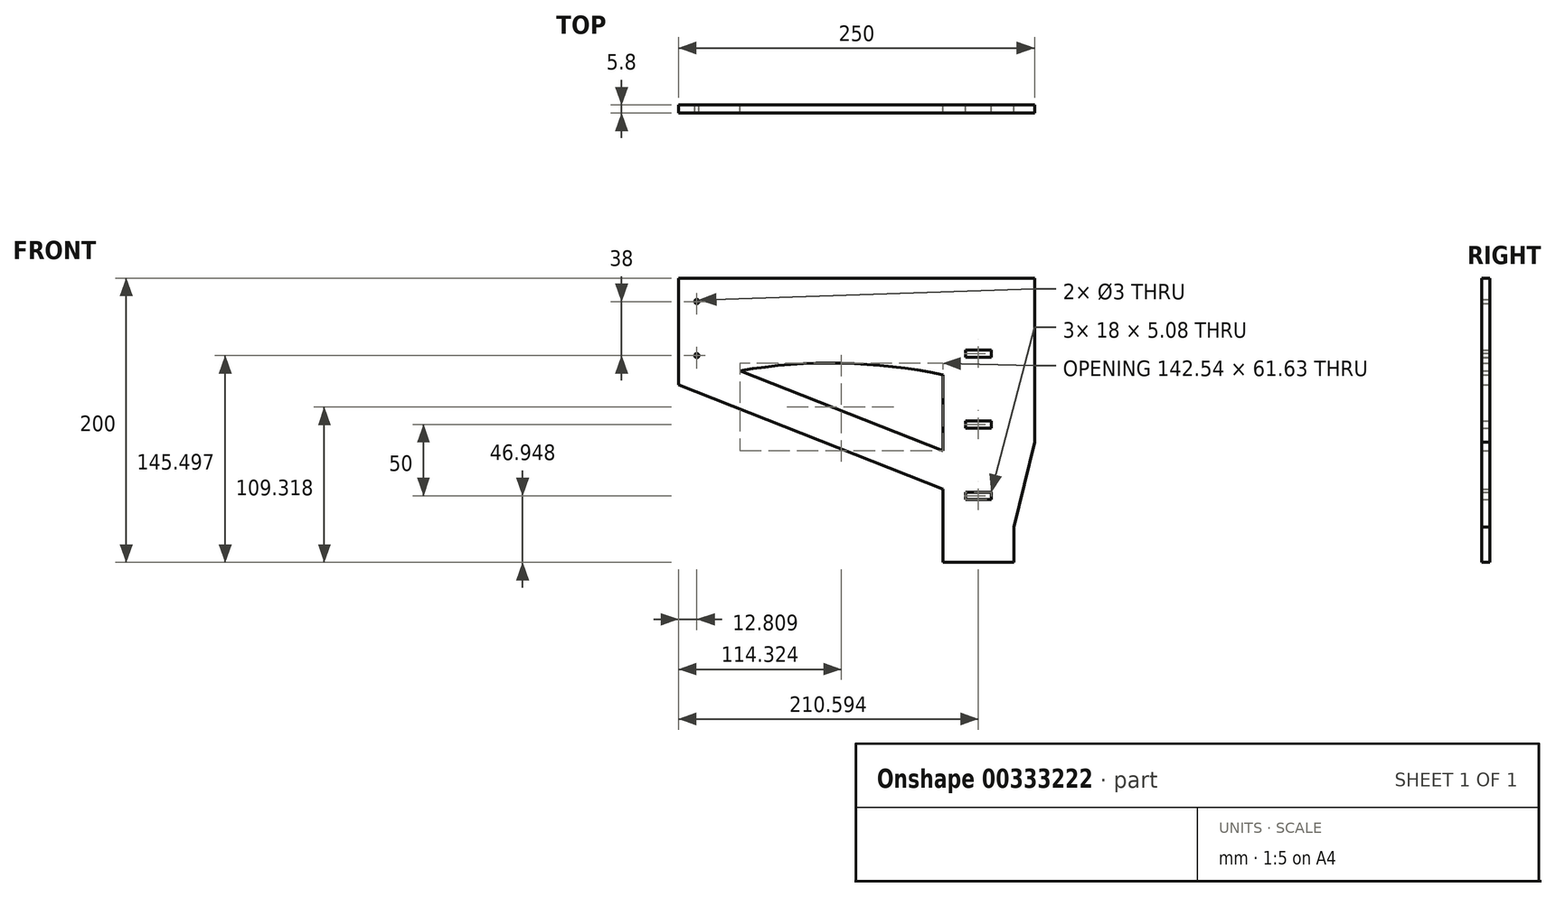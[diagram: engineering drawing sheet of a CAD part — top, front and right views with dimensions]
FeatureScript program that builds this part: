
annotation { "Feature Type Name" : "Feature", "Feature Type Description" : "" }
export const myFeature = defineFeature(function(context is Context, id is Id, definition is map)
    precondition{}
    {
        {
            var Q0;
            Q0=qCreatedBy(makeId("Front.planeOp"),FACE);
            var sketch = newSketch(context, id + "F0", { "sketchPlane" : qUnion([Q0])});
            skLineSegment(sketch, "E0.top", {"start": v(127.28, 55.74) * mm, "end": v(-122.72, 55.74) * mm});
            skLineSegment(sketch, "E0.left", {"start": v(127.28, -59.51) * mm, "end": v(127.28, 55.74) * mm});
            skLineSegment(sketch, "E0.right", {"start": v(-122.72, -19.26) * mm, "end": v(-122.72, 55.74) * mm});
            skArc(sketch, "E1", {"start": v(62.87, -12.25) * mm, "mid": v(-30.35, -4.32) * mm, "end": v(-122.72, -19.26) * mm});
            skPoint(sketch, "E2.orphan", {"position": v(-122.72, -59.51) * mm});
            skLineSegment(sketch, "E3", {"start": v(62.87, -12.25) * mm, "end": v(62.87, -119.26) * mm});
            skLineSegment(sketch, "E4", {"start": v(62.87, -119.26) * mm, "end": v(112.87, -119.26) * mm});
            skLineSegment(sketch, "E5", {"start": v(112.87, -119.26) * mm, "end": v(127.28, -59.51) * mm});
            skLineSegment(sketch, "E6", {"start": v(-122.72, -19.26) * mm, "end": v(62.87, -92.64) * mm});
            skLineSegment(sketch, "E7", {"start": v(62.87, -65.76) * mm, "end": v(-79.67, -9.4) * mm});
            skLineSegment(sketch, "E8.top", {"start": v(-122.72, 0.24) * mm, "end": v(127.28, 0.24) * mm});
            skLineSegment(sketch, "E8.left", {"start": v(-122.72, 45.49) * mm, "end": v(-122.72, 0.24) * mm});
            skLineSegment(sketch, "E9.bottom", {"start": v(-122.72, 45.49) * mm, "end": v(127.28, 45.49) * mm});
            skLineSegment(sketch, "E9.top", {"start": v(-122.72, 10.49) * mm, "end": v(127.28, 10.49) * mm});
            skLineSegment(sketch, "E9.left", {"start": v(-122.72, 45.49) * mm, "end": v(-122.72, 10.49) * mm});
            skLineSegment(sketch, "E9.right", {"start": v(127.28, 45.49) * mm, "end": v(127.28, 10.49) * mm});
            skLineSegment(sketch, "E10.direction1", {"start": v(-81.72, 10.49) * mm, "end": v(-31.72, 10.49) * mm, "construction": true});
            skLineSegment(sketch, "E11", {"start": v(-122.72, 27.99) * mm, "end": v(127.28, 27.99) * mm, "construction": true});
            skLineSegment(sketch, "E12.bottom", {"start": v(96.87, -99.85) * mm, "end": v(78.87, -99.85) * mm});
            skLineSegment(sketch, "E12.top", {"start": v(96.87, -94.77) * mm, "end": v(78.87, -94.77) * mm});
            skLineSegment(sketch, "E12.left", {"start": v(96.87, -99.85) * mm, "end": v(96.87, -94.77) * mm});
            skLineSegment(sketch, "E12.right", {"start": v(78.87, -99.85) * mm, "end": v(78.87, -94.77) * mm});
            skPoint(sketch, "E12.middle", {"position": v(87.87, -97.31) * mm});
            skPoint(sketch, "E12.middle.positionSnap0", {"position": v(87.87, -119.26) * mm});
            skPoint(sketch, "E12.centerSnap0", {"position": v(87.87, -119.26) * mm});
            skLineSegment(sketch, "E13.0.1.0", {"start": v(96.87, -44.77) * mm, "end": v(78.87, -44.77) * mm});
            skPoint(sketch, "E13.0.1.1", {"position": v(87.87, -47.31) * mm});
            skLineSegment(sketch, "E13.0.1.2", {"start": v(78.87, -49.85) * mm, "end": v(78.87, -44.77) * mm});
            skLineSegment(sketch, "E13.0.1.3", {"start": v(96.87, -49.85) * mm, "end": v(96.87, -44.77) * mm});
            skLineSegment(sketch, "E13.0.1.4", {"start": v(96.87, -49.85) * mm, "end": v(78.87, -49.85) * mm});
            skLineSegment(sketch, "E13.0.2.0", {"start": v(96.87, 5.23) * mm, "end": v(78.87, 5.23) * mm});
            skPoint(sketch, "E13.0.2.1", {"position": v(87.87, 2.69) * mm});
            skLineSegment(sketch, "E13.0.2.2", {"start": v(78.87, 0.15) * mm, "end": v(78.87, 5.23) * mm});
            skLineSegment(sketch, "E13.0.2.3", {"start": v(96.87, 0.15) * mm, "end": v(96.87, 5.23) * mm});
            skLineSegment(sketch, "E13.0.2.4", {"start": v(96.87, 0.15) * mm, "end": v(78.87, 0.15) * mm});
            skLineSegment(sketch, "E13.direction1", {"start": v(78.87, -94.77) * mm, "end": v(103.87, -94.77) * mm, "construction": true});
            skLineSegment(sketch, "E13.direction2", {"start": v(78.87, -94.77) * mm, "end": v(78.87, -44.77) * mm, "construction": true});
            skLineSegment(sketch, "E14", {"start": v(-122.72, -19.26) * mm, "end": v(-94.37, -19.26) * mm, "construction": true});
            skCircle(sketch, "E15", {"center": v(-109.91, 1.24) * mm, "radius": 1.5 * mm});
            skCircle(sketch, "E16.0.1.0", {"center": v(-109.91, 39.24) * mm, "radius": 1.5 * mm});
            skLineSegment(sketch, "E16.direction1", {"start": v(-109.91, 1.24) * mm, "end": v(-84.91, 1.24) * mm, "construction": true});
            skLineSegment(sketch, "E16.direction2", {"start": v(-109.91, 1.24) * mm, "end": v(-109.91, 39.24) * mm, "construction": true});
            skSolve(sketch);
        }
        {
            var Q0;
            Q0=qSketchRegion(id+"F0",true);
            extrude(context, id + "F1", {"entities" : qUnion([Q0]), "depth" : 5.8 * mm});
        }
        {
            var Q0;
            Q0=makeQuery(id+"F1.opExtrude","SWEPT_FACE",FACE,{"disambiguationData":[OSD([sQuery(id+"F0.wireOp",EDGE,"E4")])]});
            extrude(context, id + "F2", {"entities" : qUnion([Q0]), "operationType" : NewBodyOperationType.ADD, "depth" : 25 * mm});
        }
    });
